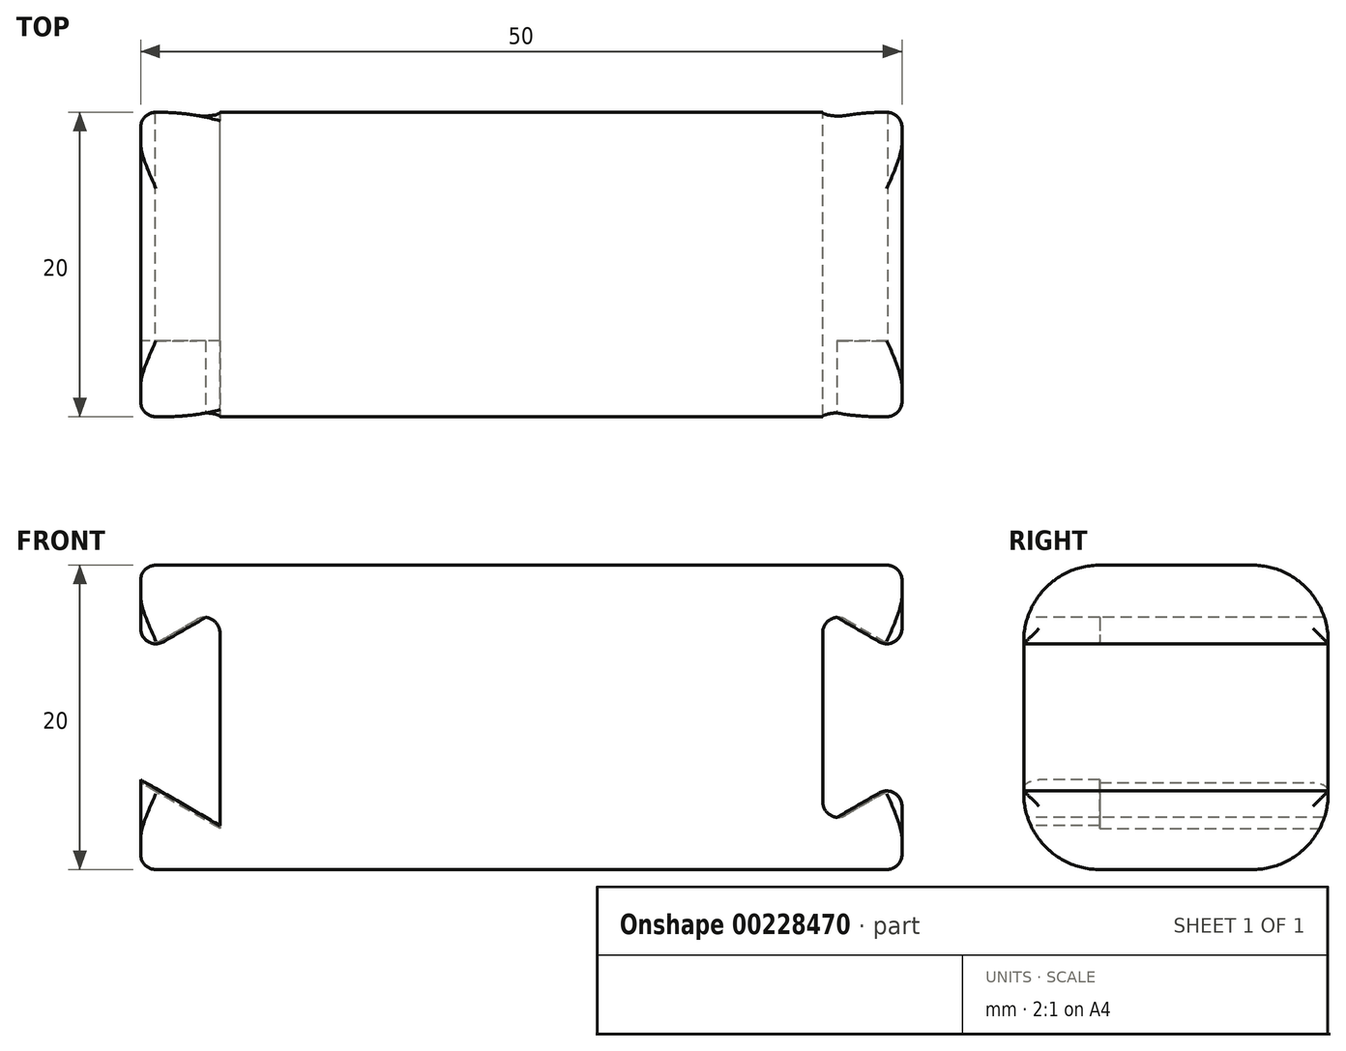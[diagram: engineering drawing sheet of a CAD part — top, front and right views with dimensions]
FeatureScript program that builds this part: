
annotation { "Feature Type Name" : "Feature", "Feature Type Description" : "" }
export const myFeature = defineFeature(function(context is Context, id is Id, definition is map)
    precondition{}
    {
        {
            var Q0;
            Q0=qCreatedBy(makeId("Right.planeOp"),FACE);
            var sketch = newSketch(context, id + "F0", { "sketchPlane" : qUnion([Q0])});
            skLineSegment(sketch, "E0.bottom", {"start": v(10, 0) * mm, "end": v(-10, 0) * mm});
            skLineSegment(sketch, "E0.top", {"start": v(10, 20) * mm, "end": v(-10, 20) * mm});
            skLineSegment(sketch, "E0.left", {"start": v(10, 0) * mm, "end": v(10, 20) * mm});
            skLineSegment(sketch, "E0.right", {"start": v(-10, 0) * mm, "end": v(-10, 20) * mm});
            skSolve(sketch);
        }
        {
            var Q0;
            Q0=makeQuery(id+"F0.imprint","IMPRINT",FACE,{"disambiguationData":[TD([[makeQuery(id+"F0.imprint","IMPRINT",EDGE,{"derivedFrom":sQuery(id+"F0.wireOp",EDGE,"E0.bottom")}),-1.0]])]});
            extrude(context, id + "F1", {"entities" : qUnion([Q0]), "depth" : 50 * mm, "offsetDistance" : 25 * mm});
        }
        {
            var Q0;
            Q0=makeQuery(id+"F1.opExtrude","SWEPT_FACE",FACE,{"disambiguationData":[OSD([sQuery(id+"F0.wireOp",EDGE,"E0.left")])]});
            var sketch = newSketch(context, id + "F2", { "sketchPlane" : qUnion([Q0])});
            skLineSegment(sketch, "E1", {"start": v(0, 5.7) * mm, "end": v(-5.2, 2.7) * mm});
            skLineSegment(sketch, "E2", {"start": v(-5.2, 2.7) * mm, "end": v(-5.2, 17.3) * mm});
            skLineSegment(sketch, "E3", {"start": v(-5.2, 17.3) * mm, "end": v(0, 14.3) * mm});
            skLineSegment(sketch, "E4", {"start": v(0, 14.3) * mm, "end": v(0, 5.7) * mm});
            skLineSegment(sketch, "E5", {"start": v(-50, 5.7) * mm, "end": v(-50, 14.3) * mm});
            skLineSegment(sketch, "E6", {"start": v(-50, 14.3) * mm, "end": v(-44.8, 17.3) * mm});
            skLineSegment(sketch, "E7", {"start": v(-44.8, 17.3) * mm, "end": v(-44.8, 2.7) * mm});
            skLineSegment(sketch, "E8", {"start": v(-44.8, 2.7) * mm, "end": v(-50, 5.7) * mm});
            skPoint(sketch, "E9", {"position": v(0, 10) * mm});
            skSolve(sketch);
        }
        {
            var Q0;
            Q0 = qSketchRegion(id + "F2", true);
            extrude(context, id + "F3", {"entities" : qUnion([Q0]), "operationType" : NewBodyOperationType.REMOVE, "oppositeDirection" : true, "depth" : 25 * mm, "offsetDistance" : 25 * mm});
        }
        {
            var Q0;
            Q0=makeQuery(id+"F1.opExtrude","SWEPT_FACE",FACE,{"disambiguationData":[OSD([sQuery(id+"F0.wireOp",EDGE,"E0.right")])]});
            var sketch = newSketch(context, id + "F4", { "sketchPlane" : qUnion([Q0])});
            skLineSegment(sketch, "E10", {"start": v(0, 14.3) * mm, "end": v(5.2, 17.3) * mm});
            skLineSegment(sketch, "E11", {"start": v(5.2, 17.3) * mm, "end": v(5.2, 17.1) * mm});
            skLineSegment(sketch, "E12", {"start": v(5.2, 17.1) * mm, "end": v(0, 14.1) * mm});
            skLineSegment(sketch, "E13", {"start": v(0, 14.1) * mm, "end": v(0, 14.3) * mm});
            skLineSegment(sketch, "E14", {"start": v(0, 5.7) * mm, "end": v(0, 5.9) * mm});
            skLineSegment(sketch, "E15", {"start": v(0, 5.9) * mm, "end": v(5.2, 2.9) * mm});
            skLineSegment(sketch, "E16", {"start": v(5.2, 2.9) * mm, "end": v(5.2, 2.7) * mm});
            skLineSegment(sketch, "E17", {"start": v(5.2, 2.7) * mm, "end": v(0, 5.7) * mm});
            skLineSegment(sketch, "E18", {"start": v(50, 14.3) * mm, "end": v(44.8, 17.3) * mm});
            skLineSegment(sketch, "E19", {"start": v(44.8, 17.3) * mm, "end": v(44.8, 17.1) * mm});
            skLineSegment(sketch, "E20", {"start": v(44.8, 17.1) * mm, "end": v(50, 14.1) * mm});
            skLineSegment(sketch, "E21", {"start": v(50, 14.1) * mm, "end": v(50, 14.3) * mm});
            skLineSegment(sketch, "E22", {"start": v(50, 5.7) * mm, "end": v(44.8, 2.7) * mm});
            skLineSegment(sketch, "E23", {"start": v(50, 5.9) * mm, "end": v(50, 5.7) * mm});
            skLineSegment(sketch, "E24", {"start": v(50, 5.9) * mm, "end": v(44.8, 2.9) * mm});
            skLineSegment(sketch, "E25", {"start": v(44.8, 2.9) * mm, "end": v(44.8, 2.7) * mm});
            skSolve(sketch);
        }
        {
            var Q0;
            Q0 = qSketchRegion(id + "F4", true);
            extrude(context, id + "F5", {"entities" : qUnion([Q0]), "operationType" : NewBodyOperationType.ADD, "oppositeDirection" : true, "depth" : 5 * mm, "offsetDistance" : 25 * mm});
        }
        {
            var Q0;
            Q0=makeQuery(id+"F3.boolean.opBoolean","COPY",EDGE,{"derivedFrom":makeQuery(id+"F3.opExtrude","SWEPT_EDGE",EDGE,{"disambiguationData":[OSD([sQuery(id+"F2.wireOp",EDGE,"E2"),sQuery(id+"F2.wireOp",EDGE,"E3")])]})});
            var Q1;
            Q1=makeQuery(id+"F5.opExtrude","SWEPT_EDGE",EDGE,{"disambiguationData":[OSD([sQuery(id+"F4.wireOp",EDGE,"E12"),sQuery(id+"F4.wireOp",EDGE,"E13")])]});
            var Q2;
            Q2=makeQuery(id+"F5.opExtrude","SWEPT_EDGE",EDGE,{"disambiguationData":[OSD([sQuery(id+"F0.wireOp",EDGE,"E0.right"),sQuery(id+"F2.wireOp",EDGE,"E2"),sQuery(id+"F4.wireOp",EDGE,"E15"),sQuery(id+"F4.wireOp",EDGE,"E16")])]});
            var Q3;
            Q3=makeQuery(id+"F3.boolean.opBoolean","COPY",EDGE,{"derivedFrom":makeQuery(id+"F3.opExtrude","SWEPT_EDGE",EDGE,{"disambiguationData":[OSD([sQuery(id+"F0.wireOp",EDGE,"E0.left"),sQuery(id+"F2.wireOp",EDGE,"E1"),sQuery(id+"F2.wireOp",EDGE,"E4")])]})});
            var Q4;
            Q4=makeQuery(id+"F3.boolean.opBoolean","COPY",EDGE,{"derivedFrom":makeQuery(id+"F3.opExtrude","SWEPT_EDGE",EDGE,{"disambiguationData":[OSD([sQuery(id+"F2.wireOp",EDGE,"E6"),sQuery(id+"F2.wireOp",EDGE,"E7")])]})});
            var Q5;
            Q5=makeQuery(id+"F5.opExtrude","SWEPT_EDGE",EDGE,{"disambiguationData":[OSD([sQuery(id+"F4.wireOp",EDGE,"E20"),sQuery(id+"F4.wireOp",EDGE,"E21")])]});
            var Q6;
            Q6=makeQuery(id+"F3.boolean.opBoolean","COPY",EDGE,{"derivedFrom":makeQuery(id+"F3.opExtrude","SWEPT_EDGE",EDGE,{"disambiguationData":[OSD([sQuery(id+"F2.wireOp",EDGE,"E7"),sQuery(id+"F2.wireOp",EDGE,"E8")])]})});
            var Q7;
            Q7=makeQuery(id+"F5.opExtrude","SWEPT_EDGE",EDGE,{"disambiguationData":[OSD([sQuery(id+"F4.wireOp",EDGE,"E23"),sQuery(id+"F4.wireOp",EDGE,"E24")])]});
            var Q8;
            Q8=makeQuery(id+"F1.opExtrude","CAP_EDGE",EDGE,{"disambiguationData":[OSD([sQuery(id+"F0.wireOp",EDGE,"E0.top")])],"isStart":false});
            var Q9;
            {var subQ0=sQuery(id+"F0.wireOp",EDGE,"E0.right");var subQ1=sQuery(id+"F0.wireOp",EDGE,"E0.top");Q9=makeQuery(id+"F5.boolean.opBoolean","MERGE",EDGE,{"derivedFrom":[makeQuery(id+"F3.boolean.opBoolean","SPLIT",EDGE,{"disambiguationData":[TD([makeQuery(id+"F1.opExtrude","SWEPT_FACE",FACE,{"disambiguationData":[OSD([subQ1])]})])],"derivedFrom":makeQuery(id+"F1.opExtrude","CAP_EDGE",EDGE,{"disambiguationData":[OSD([subQ0])],"isStart":false})}),makeQuery(id+"F5.opExtrude","CAP_EDGE",EDGE,{"disambiguationData":[OSD([sQuery(id+"F4.wireOp",EDGE,"E21")])],"isStart":true})]});}
            var Q10;
            {var subQ0=sQuery(id+"F0.wireOp",EDGE,"E0.left");var subQ1=sQuery(id+"F0.wireOp",EDGE,"E0.top");Q10=makeQuery(id+"F3.boolean.opBoolean","SPLIT",EDGE,{"disambiguationData":[TD([makeQuery(id+"F1.opExtrude","SWEPT_FACE",FACE,{"disambiguationData":[OSD([subQ1])]})])],"derivedFrom":makeQuery(id+"F1.opExtrude","CAP_EDGE",EDGE,{"disambiguationData":[OSD([subQ0])],"isStart":false})});}
            var Q11;
            {var subQ0=sQuery(id+"F0.wireOp",EDGE,"E0.bottom");var subQ1=sQuery(id+"F0.wireOp",EDGE,"E0.left");Q11=makeQuery(id+"F3.boolean.opBoolean","SPLIT",EDGE,{"disambiguationData":[TD([makeQuery(id+"F1.opExtrude","SWEPT_FACE",FACE,{"disambiguationData":[OSD([subQ0])]})])],"derivedFrom":makeQuery(id+"F1.opExtrude","CAP_EDGE",EDGE,{"disambiguationData":[OSD([subQ1])],"isStart":false})});}
            var Q12;
            Q12=makeQuery(id+"F1.opExtrude","CAP_EDGE",EDGE,{"disambiguationData":[OSD([sQuery(id+"F0.wireOp",EDGE,"E0.bottom")])],"isStart":false});
            var Q13;
            {var subQ0=sQuery(id+"F0.wireOp",EDGE,"E0.bottom");var subQ1=sQuery(id+"F0.wireOp",EDGE,"E0.right");Q13=makeQuery(id+"F5.boolean.opBoolean","MERGE",EDGE,{"derivedFrom":[makeQuery(id+"F3.boolean.opBoolean","SPLIT",EDGE,{"disambiguationData":[TD([makeQuery(id+"F1.opExtrude","SWEPT_FACE",FACE,{"disambiguationData":[OSD([subQ0])]})])],"derivedFrom":makeQuery(id+"F1.opExtrude","CAP_EDGE",EDGE,{"disambiguationData":[OSD([subQ1])],"isStart":false})}),makeQuery(id+"F5.opExtrude","CAP_EDGE",EDGE,{"disambiguationData":[OSD([sQuery(id+"F4.wireOp",EDGE,"E23")])],"isStart":true})]});}
            var Q14;
            Q14=makeQuery(id+"F1.opExtrude","CAP_EDGE",EDGE,{"disambiguationData":[OSD([sQuery(id+"F0.wireOp",EDGE,"E0.top")])],"isStart":true});
            var Q15;
            {var subQ0=sQuery(id+"F0.wireOp",EDGE,"E0.right");var subQ1=sQuery(id+"F0.wireOp",EDGE,"E0.top");Q15=makeQuery(id+"F5.boolean.opBoolean","MERGE",EDGE,{"derivedFrom":[makeQuery(id+"F3.boolean.opBoolean","SPLIT",EDGE,{"disambiguationData":[TD([makeQuery(id+"F1.opExtrude","SWEPT_FACE",FACE,{"disambiguationData":[OSD([subQ1])]})])],"derivedFrom":makeQuery(id+"F1.opExtrude","CAP_EDGE",EDGE,{"disambiguationData":[OSD([subQ0])],"isStart":true})}),makeQuery(id+"F5.opExtrude","CAP_EDGE",EDGE,{"disambiguationData":[OSD([sQuery(id+"F4.wireOp",EDGE,"E13")])],"isStart":true})]});}
            var Q16;
            {var subQ0=sQuery(id+"F0.wireOp",EDGE,"E0.left");var subQ1=sQuery(id+"F0.wireOp",EDGE,"E0.top");Q16=makeQuery(id+"F3.boolean.opBoolean","SPLIT",EDGE,{"disambiguationData":[TD([makeQuery(id+"F1.opExtrude","SWEPT_FACE",FACE,{"disambiguationData":[OSD([subQ1])]})])],"derivedFrom":makeQuery(id+"F1.opExtrude","CAP_EDGE",EDGE,{"disambiguationData":[OSD([subQ0])],"isStart":true})});}
            var Q17;
            {var subQ0=sQuery(id+"F0.wireOp",EDGE,"E0.bottom");var subQ1=sQuery(id+"F0.wireOp",EDGE,"E0.left");Q17=makeQuery(id+"F3.boolean.opBoolean","SPLIT",EDGE,{"disambiguationData":[TD([makeQuery(id+"F1.opExtrude","SWEPT_FACE",FACE,{"disambiguationData":[OSD([subQ0])]})])],"derivedFrom":makeQuery(id+"F1.opExtrude","CAP_EDGE",EDGE,{"disambiguationData":[OSD([subQ1])],"isStart":true})});}
            var Q18;
            Q18=makeQuery(id+"F1.opExtrude","CAP_EDGE",EDGE,{"disambiguationData":[OSD([sQuery(id+"F0.wireOp",EDGE,"E0.bottom")])],"isStart":true});
            var Q19;
            {var subQ0=sQuery(id+"F0.wireOp",EDGE,"E0.bottom");var subQ1=sQuery(id+"F0.wireOp",EDGE,"E0.right");Q19=makeQuery(id+"F5.boolean.opBoolean","MERGE",EDGE,{"derivedFrom":[makeQuery(id+"F3.boolean.opBoolean","SPLIT",EDGE,{"disambiguationData":[TD([makeQuery(id+"F1.opExtrude","SWEPT_FACE",FACE,{"disambiguationData":[OSD([subQ0])]})])],"derivedFrom":makeQuery(id+"F1.opExtrude","CAP_EDGE",EDGE,{"disambiguationData":[OSD([subQ1])],"isStart":true})}),makeQuery(id+"F5.opExtrude","CAP_EDGE",EDGE,{"disambiguationData":[OSD([sQuery(id+"F4.wireOp",EDGE,"E14")])],"isStart":true})]});}
            fillet(context, id + "F6", {"entities" : qUnion([Q0, Q1, Q2, Q3, Q4, Q5, Q6, Q7, Q8, Q9, Q10, Q11, Q12, Q13, Q14, Q15, Q16, Q17, Q18, Q19]), "tangentPropagation" : true, "radius" : 1 * mm, "defaultsChanged" : true, "vertexSettings" : [], "allowEdgeOverflow" : false});
        }
        {
            var Q0;
            Q0=makeQuery(id+"F3.boolean.opBoolean","COPY",FACE,{"derivedFrom":makeQuery(id+"F3.opExtrude","SWEPT_FACE",FACE,{"disambiguationData":[OSD([sQuery(id+"F2.wireOp",EDGE,"E2")])]})});
            var sketch = newSketch(context, id + "F7", { "sketchPlane" : qUnion([Q0])});
            skLineSegment(sketch, "E26.bottom", {"start": v(-5, 0) * mm, "end": v(5, 0) * mm});
            skLineSegment(sketch, "E26.top", {"start": v(-5, 20) * mm, "end": v(5, 20) * mm});
            skLineSegment(sketch, "E26.left", {"start": v(-10, 5) * mm, "end": v(-10, 15) * mm});
            skLineSegment(sketch, "E26.right", {"start": v(10, 5) * mm, "end": v(10, 15) * mm});
            skPoint(sketch, "E27.visualSharp", {"position": v(-10, 20) * mm});
            skArc(sketch, "E27.filletArc", {"start": v(-5, 20) * mm, "mid": v(-8.54, 18.54) * mm, "end": v(-10, 15) * mm});
            skPoint(sketch, "E28.visualSharp", {"position": v(10, 20) * mm});
            skArc(sketch, "E28.filletArc", {"start": v(10, 15) * mm, "mid": v(8.54, 18.54) * mm, "end": v(5, 20) * mm});
            skPoint(sketch, "E29.visualSharp", {"position": v(10, 0) * mm});
            skArc(sketch, "E29.filletArc", {"start": v(5, 0) * mm, "mid": v(8.54, 1.46) * mm, "end": v(10, 5) * mm});
            skPoint(sketch, "E30.visualSharp", {"position": v(-10, 0) * mm});
            skArc(sketch, "E30.filletArc", {"start": v(-10, 5) * mm, "mid": v(-8.54, 1.46) * mm, "end": v(-5, 0) * mm});
            skSolve(sketch);
        }
        {
            var Q0;
            Q0 = qSketchRegion(id + "F7", true);
            extrude(context, id + "F8", {"entities" : qUnion([Q0]), "operationType" : NewBodyOperationType.INTERSECT, "oppositeDirection" : true, "depth" : 50 * mm, "offsetDistance" : 25 * mm, "hasSecondDirection" : true, "secondDirectionOppositeDirection" : false, "secondDirectionDepth" : 25 * mm});
        }
    });
